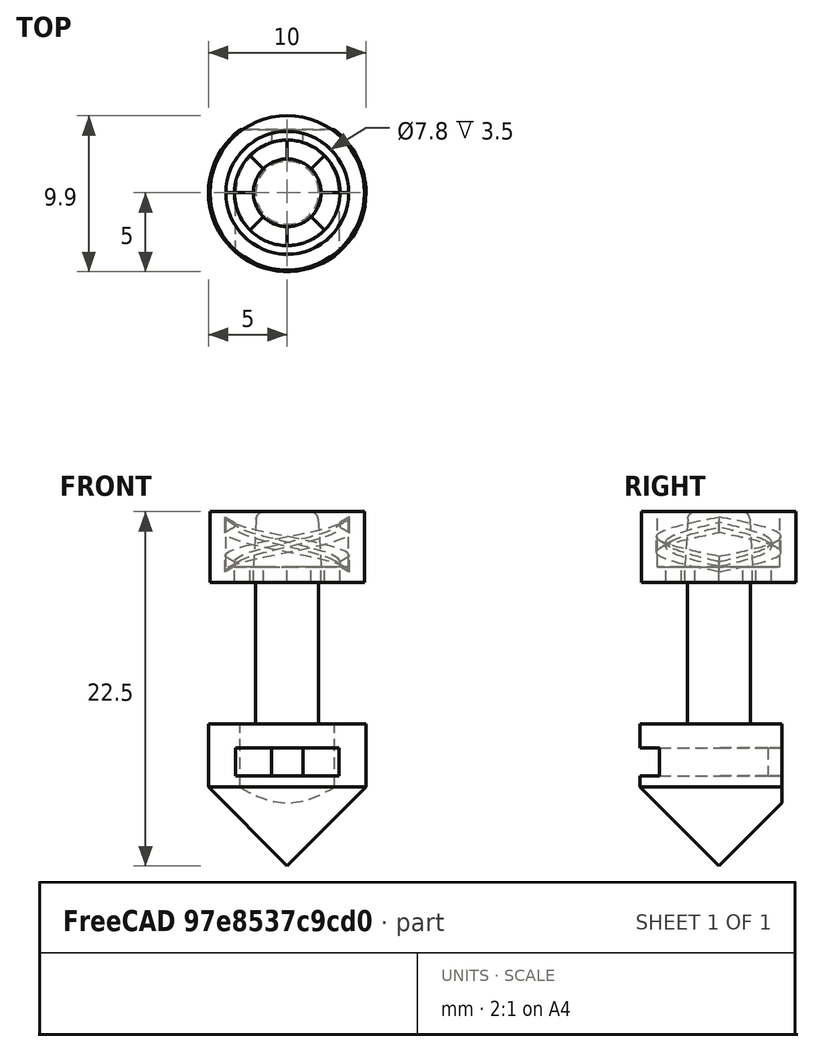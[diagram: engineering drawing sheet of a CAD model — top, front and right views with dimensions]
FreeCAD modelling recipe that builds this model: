
FCSTD DOCUMENT  (FreeCAD 0.19R24344 (Git))
Label: Adapter_Magnet_Luer
Comment: An adapter between the magnet keyed form and a Luer lock for blunt syringe tips.
License: Creative Commons Attribution-NonCommercial-ShareAlike
LicenseURL: http://creativecommons.org/licenses/by-nc-sa/4.0/
objects: Sketcher::SketchObject×12, PartDesign::Pocket×6, PartDesign::Body×4, PartDesign::Revolution×2, PartDesign::ShapeBinder×2, PartDesign::AdditivePipe×2, Mesh::Feature×1
note: 38 computed .brp shape members not serialized (recipe doc carries the construction recipe); baked Part::Feature solids carry a one-line shape summary decoded from their .brp

FEATURE [Sketcher::SketchObject] Sketch
  FullyConstrained = false
  MapMode = 5
  Placement = pos=(0,0,0) rot=(1,0,0;1.5708rad)
  Support = -> [XZ_Plane]
  sketch-geometry (9):
    g0: LineSegment StartX=0 StartY=4.5 StartZ=0 EndX=1.46876 EndY=4.5 EndZ=0
    g1: LineSegment StartX=1.96786 StartY=4.03 StartZ=0 EndX=2.15 EndY=1 EndZ=0
    g2: LineSegment StartX=2.15 StartY=1 StartZ=0 EndX=3.9 EndY=1 EndZ=0
    g3: LineSegment StartX=3.9 StartY=1 StartZ=0 EndX=3.9 EndY=4.5 EndZ=0
    g4: LineSegment StartX=3.9 StartY=4.5 StartZ=0 EndX=4.9 EndY=4.5 EndZ=0
    g5: LineSegment StartX=4.9 StartY=4.5 StartZ=0 EndX=4.9 EndY=0 EndZ=0
    g6: LineSegment StartX=4.9 StartY=0 StartZ=0 EndX=0 EndY=0 EndZ=0
    g7: LineSegment StartX=0 StartY=0 StartZ=0 EndX=0 EndY=4.5 EndZ=0
    g8: ArcOfCircle CenterX=1.46876 CenterY=4 CenterZ=0 NormalX=0 NormalY=0 NormalZ=1 AngleXU=0 Radius=0.5 StartAngle=0.0600393 EndAngle=1.5708
  constraints (25):
    c: PointOnObject(g0,g-2)
    c: Horizontal(g0)
    c: Coincident(g2,g1)
    c: Horizontal(g2)
    c: Coincident(g3,g2)
    c: Vertical(g3)
    c: Coincident(g4,g3)
    c: Horizontal(g4)
    c: Coincident(g5,g4)
    c: PointOnObject(g5,g-1)
    c: Vertical(g5)
    c: Coincident(g6,g5)
    c: Coincident(g6,g-1)
    c: Coincident(g7,g6)
    c: Coincident(g7,g0)
    c: Angle(g0,g1) = 1.63084
    c: DistanceX(g-1,g3) = 3.9
    c: DistanceX(g4,g4) = 1
    c: DistanceY(g3,g3) = 3.5
    c: DistanceY(g5,g5) = 4.5
    c: Tangent(g0,g8) = 1.5708
    c: Tangent(g1,g8) = 1.5708
    c: Radius(g8) = 0.5
    c: DistanceX(g-1,g1) = 2.15
    c: DistanceY(g-1,g0) = 4.5
FEATURE [PartDesign::Revolution] Revolution
  AllowMultiFace = false
  Angle = 360
  Axis = (0,2e-16,1)
  Base = (0,0,0)
  Placement = pos=(0,0,0) rot=(1,0,0;1.5708rad)
  Profile = -> Sketch
  ReferenceAxis = -> Sketch [V_Axis]
  Reversed = true
FEATURE [Sketcher::SketchObject] Sketch001
  FullyConstrained = false
  MapMode = 5
  Placement = pos=(0,0,0) rot=(1,0,0;1.5708rad)
  Support = -> [XZ_Plane]
  sketch-geometry (4):
    g0: LineSegment StartX=3.35 StartY=3.95257 StartZ=0 EndX=3.35 EndY=3.65257 EndZ=0
    g1: LineSegment StartX=3.35 StartY=3.65257 StartZ=0 EndX=3.95 EndY=3.30616 EndZ=0
    g2: LineSegment StartX=3.95 StartY=3.30616 StartZ=0 EndX=3.95 EndY=4.29898 EndZ=0
    g3: LineSegment StartX=3.95 StartY=4.29898 StartZ=0 EndX=3.35 EndY=3.95257 EndZ=0
  constraints (11):
    c: Vertical(g0)
    c: Coincident(g1,g0)
    c: Coincident(g2,g1)
    c: Vertical(g2)
    c: Coincident(g3,g0)
    c: Angle(g0,g3) = 2.0944
    c: Coincident(g2,g3)
    c: Angle(g1,g0) = 2.0944
    c: DistanceY(g0,g0) = 0.3
    c: DistanceX(g0,g2) = 0.6
    c: DistanceX(g-1,g0) = 3.35
FEATURE [Sketcher::SketchObject] Sketch002
  FullyConstrained = false
  MapMode = 5
  Placement = pos=(0,0,0) rot=(1,0,0;3.14159rad)
  Support = -> [Revolution]
  sketch-geometry (5):
    g0: LineSegment StartX=-2.15 StartY=3e-16 StartZ=0 EndX=-3.35 EndY=4e-16 EndZ=0
    g1: ArcOfCircle CenterX=0 CenterY=0 CenterZ=0 NormalX=0 NormalY=0 NormalZ=1 AngleXU=0 Radius=2.15 StartAngle=2.35619 EndAngle=3.14159
    g2: ArcOfCircle CenterX=0 CenterY=0 CenterZ=0 NormalX=0 NormalY=0 NormalZ=1 AngleXU=0 Radius=3.35 StartAngle=2.35619 EndAngle=3.14159
    g3: LineSegment StartX=-2.36881 StartY=2.36881 StartZ=0 EndX=-1.52028 EndY=1.52028 EndZ=0
    g4: LineSegment StartX=-2.36881 StartY=2.36881 StartZ=0 EndX=0 EndY=0 EndZ=0
  constraints (14):
    c: PointOnObject(g0,g-1)
    c: PointOnObject(g0,g-1)
    c: Coincident(g2,g0)
    c: Coincident(g1,g0)
    c: Coincident(g2,g3)
    c: Coincident(g3,g1)
    c: Coincident(g1,g-1)
    c: Coincident(g2,g1)
    c: Radius(g2) = 3.35
    c: Radius(g1) = 2.15
    c: Coincident(g4,g2)
    c: Coincident(g4,g1)
    c: Parallel(g4,g3)
    c: Angle(g3,g0) = 0.785398
FEATURE [Sketcher::SketchObject] Sketch003
  FullyConstrained = false
  MapMode = 5
  Placement = pos=(0,0,0) rot=(1,0,0;3.14159rad)
  Support = -> [Revolution]
  sketch-geometry (5):
    g0: LineSegment StartX=1e-16 StartY=2.15 StartZ=0 EndX=2e-16 EndY=3.35 EndZ=0
    g1: ArcOfCircle CenterX=0 CenterY=0 CenterZ=0 NormalX=0 NormalY=0 NormalZ=1 AngleXU=0 Radius=2.15 StartAngle=0.785398 EndAngle=1.5708
    g2: ArcOfCircle CenterX=0 CenterY=0 CenterZ=0 NormalX=0 NormalY=0 NormalZ=1 AngleXU=0 Radius=3.35 StartAngle=0.785398 EndAngle=1.5708
    g3: LineSegment StartX=2.36881 StartY=2.36881 StartZ=0 EndX=1.52028 EndY=1.52028 EndZ=0
    g4: LineSegment StartX=2.36881 StartY=2.36881 StartZ=0 EndX=0 EndY=0 EndZ=0
  constraints (14):
    c: Coincident(g2,g3)
    c: Coincident(g3,g1)
    c: Coincident(g1,g-1)
    c: Coincident(g2,g1)
    c: Radius(g2) = 3.35
    c: Radius(g1) = 2.15
    c: Coincident(g4,g2)
    c: Coincident(g4,g1)
    c: Parallel(g4,g3)
    c: Angle(g3,g0) = 0.785398
    c: Coincident(g0,g2)
    c: Coincident(g1,g0)
    c: PointOnObject(g0,g-2)
    c: PointOnObject(g0,g-2)
FEATURE [Sketcher::SketchObject] Sketch004
  FullyConstrained = false
  MapMode = 5
  Placement = pos=(0,0,0) rot=(1,0,0;3.14159rad)
  Support = -> [Revolution]
  sketch-geometry (5):
    g0: LineSegment StartX=2.15 StartY=0 StartZ=0 EndX=3.35 EndY=-8e-16 EndZ=0
    g1: ArcOfCircle CenterX=0 CenterY=0 CenterZ=0 NormalX=0 NormalY=0 NormalZ=1 AngleXU=0 Radius=2.15 StartAngle=5.49779 EndAngle=6.28319
    g2: ArcOfCircle CenterX=0 CenterY=0 CenterZ=0 NormalX=0 NormalY=0 NormalZ=1 AngleXU=0 Radius=3.35 StartAngle=5.49779 EndAngle=6.28319
    g3: LineSegment StartX=2.36881 StartY=-2.36881 StartZ=0 EndX=1.52028 EndY=-1.52028 EndZ=0
    g4: LineSegment StartX=2.36881 StartY=-2.36881 StartZ=0 EndX=0 EndY=0 EndZ=0
  constraints (14):
    c: Coincident(g2,g0)
    c: Coincident(g1,g0)
    c: Coincident(g2,g3)
    c: Coincident(g3,g1)
    c: Coincident(g1,g-1)
    c: Coincident(g2,g1)
    c: Radius(g2) = 3.35
    c: Radius(g1) = 2.15
    c: Coincident(g4,g2)
    c: Coincident(g4,g1)
    c: Parallel(g4,g3)
    c: Angle(g3,g0) = 0.785398
    c: PointOnObject(g0,g-1)
    c: PointOnObject(g0,g-1)
FEATURE [Sketcher::SketchObject] Sketch005
  FullyConstrained = false
  MapMode = 5
  Placement = pos=(0,0,0) rot=(1,0,0;3.14159rad)
  Support = -> [Revolution]
  sketch-geometry (5):
    g0: LineSegment StartX=-4e-16 StartY=-2.15 StartZ=0 EndX=-6e-16 EndY=-3.35 EndZ=0
    g1: ArcOfCircle CenterX=0 CenterY=0 CenterZ=0 NormalX=0 NormalY=0 NormalZ=1 AngleXU=0 Radius=2.15 StartAngle=3.92699 EndAngle=4.71239
    g2: ArcOfCircle CenterX=0 CenterY=0 CenterZ=0 NormalX=0 NormalY=0 NormalZ=1 AngleXU=0 Radius=3.35 StartAngle=3.92699 EndAngle=4.71239
    g3: LineSegment StartX=-2.36881 StartY=-2.36881 StartZ=0 EndX=-1.52028 EndY=-1.52028 EndZ=0
    g4: LineSegment StartX=-2.36881 StartY=-2.36881 StartZ=0 EndX=0 EndY=0 EndZ=0
  constraints (14):
    c: Coincident(g2,g0)
    c: Coincident(g1,g0)
    c: Coincident(g2,g3)
    c: Coincident(g3,g1)
    c: Coincident(g1,g-1)
    c: Coincident(g2,g1)
    c: Radius(g2) = 3.35
    c: Radius(g1) = 2.15
    c: Coincident(g4,g2)
    c: Coincident(g4,g1)
    c: Parallel(g4,g3)
    c: Angle(g3,g0) = 0.785398
    c: PointOnObject(g0,g-2)
    c: PointOnObject(g0,g-2)
FEATURE [PartDesign::Pocket] Pocket
  AllowMultiFace = false
  BaseFeature = -> Revolution
  Length = 5
  Length2 = 100
  Placement = pos=(0,0,0) rot=(1,0,0;1.5708rad)
  Profile = -> Sketch002
  Type = 1
FEATURE [PartDesign::Pocket] Pocket001
  AllowMultiFace = false
  BaseFeature = -> Pocket
  Length = 5
  Length2 = 100
  Placement = pos=(0,0,0) rot=(1,0,0;1.5708rad)
  Profile = -> Sketch003
  Type = 1
FEATURE [PartDesign::Pocket] Pocket002
  AllowMultiFace = false
  BaseFeature = -> Pocket001
  Length = 5
  Length2 = 100
  Placement = pos=(0,0,0) rot=(1,0,0;1.5708rad)
  Profile = -> Sketch004
  Type = 1
FEATURE [PartDesign::Pocket] Pocket003
  AllowMultiFace = false
  BaseFeature = -> Pocket002
  Length = 5
  Length2 = 100
  Placement = pos=(0,0,0) rot=(1,0,0;1.5708rad)
  Profile = -> Sketch005
  Type = 1
FEATURE [Sketcher::SketchObject] Sketch006
  FullyConstrained = true
  MapMode = 5
  Placement = pos=(0,0,0) rot=(1,0,0;3.14159rad)
  Support = -> [Pocket003]
FEATURE [PartDesign::Body] Body  label="Luer body"
  Group = -> [Sketch,Revolution,Sketch001,Pocket,Pocket001,Pocket002,Pocket003,Sketch006]
  Origin = -> Origin
  Tip = -> Pocket003
FEATURE [Sketcher::SketchObject] Sketch007
  FullyConstrained = false
  MapMode = 5
  Placement = pos=(0,0,0) rot=(1,0,0;1.5708rad)
  Support = -> [XZ_Plane004]
  sketch-geometry (6):
    g0: LineSegment StartX=0 StartY=0 StartZ=0 EndX=0 EndY=-18 EndZ=0
    g1: LineSegment StartX=0 StartY=-18 StartZ=0 EndX=5 EndY=-13 EndZ=0
    g2: LineSegment StartX=5 StartY=-13 StartZ=0 EndX=5 EndY=-9 EndZ=0
    g3: LineSegment StartX=5 StartY=-9 StartZ=0 EndX=2 EndY=-9 EndZ=0
    g4: LineSegment StartX=2 StartY=-9 StartZ=0 EndX=2 EndY=0 EndZ=0
    g5: LineSegment StartX=2 StartY=0 StartZ=0 EndX=0 EndY=0 EndZ=0
  constraints (17):
    c: Coincident(g0,g-1)
    c: Vertical(g0)
    c: Coincident(g1,g0)
    c: Coincident(g2,g1)
    c: Vertical(g2)
    c: Horizontal(g3)
    c: PointOnObject(g4,g-1)
    c: Vertical(g4)
    c: Coincident(g5,g4)
    c: Coincident(g5,g0)
    c: Coincident(g2,g3)
    c: Coincident(g3,g4)
    c: DistanceY(g4,g4) = 9
    c: DistanceX(g-1,g2) = 5
    c: DistanceY(g2,g2) = 4
    c: DistanceY(g0,g1) = 5
    c: DistanceX(g-1,g3) = 2
FEATURE [PartDesign::Revolution] Revolution001
  AllowMultiFace = false
  Angle = 360
  Axis = (0,2e-16,1)
  Base = (0,0,0)
  Placement = pos=(0,0,0) rot=(1,0,0;1.5708rad)
  Profile = -> Sketch007
  ReferenceAxis = -> Sketch007 [V_Axis]
  Reversed = true
FEATURE [Sketcher::SketchObject] Sketch008
  FullyConstrained = false
  MapMode = 5
  Placement = pos=(0,-4e-15,-9) rot=(0,0,1;3.14159rad)
  Support = -> [Revolution001]
  sketch-geometry (4):
    g0: LineSegment StartX=-5 StartY=-4 StartZ=0 EndX=5 EndY=-4 EndZ=0
    g1: LineSegment StartX=5 StartY=-4 StartZ=0 EndX=5 EndY=-5.5 EndZ=0
    g2: LineSegment StartX=5 StartY=-5.5 StartZ=0 EndX=-5 EndY=-5.5 EndZ=0
    g3: LineSegment StartX=-5 StartY=-5.5 StartZ=0 EndX=-5 EndY=-4 EndZ=0
  constraints (12):
    c: Coincident(g0,g1)
    c: Coincident(g1,g2)
    c: Coincident(g2,g3)
    c: Coincident(g3,g0)
    c: Horizontal(g0)
    c: Horizontal(g2)
    c: Vertical(g1)
    c: Vertical(g3)
    c: DistanceY(g0,g-1) = 4
    c: Distance(g0) = 10
    c: Distance(g3) = 1.5
    c: DistanceX(g2,g-1) = 5
FEATURE [PartDesign::Pocket] Pocket004
  AllowMultiFace = false
  BaseFeature = -> Revolution001
  Length = 5
  Length2 = 100
  Placement = pos=(0,0,0) rot=(1,0,0;1.5708rad)
  Profile = -> Sketch008
  Type = 1
FEATURE [Sketcher::SketchObject] Sketch009
  AttachmentOffset = pos=(0,0,-1.5) rot=(0,0,1;0rad)
  FullyConstrained = false
  MapMode = 5
  Placement = pos=(0,-4.6e-15,-10.5) rot=(0,0,1;3.14159rad)
  Support = -> [Pocket004]
  sketch-geometry (8):
    g0: ArcOfCircle CenterX=0 CenterY=0 CenterZ=0 NormalX=0 NormalY=0 NormalZ=1 AngleXU=0 Radius=3.275 StartAngle=3.14159 EndAngle=4.40209
    g1: LineSegment StartX=-3.275 StartY=4e-16 StartZ=0 EndX=-3.275 EndY=6.5 EndZ=0
    g2: LineSegment StartX=-3.275 StartY=6.5 StartZ=0 EndX=3.27 EndY=6.5 EndZ=0
    g3: LineSegment StartX=3.27 StartY=6.5 StartZ=0 EndX=3.27 EndY=-9e-16 EndZ=0
    g4: ArcOfCircle CenterX=0 CenterY=0 CenterZ=0 NormalX=0 NormalY=0 NormalZ=1 AngleXU=0 Radius=3.27 StartAngle=5.02318 EndAngle=6.28319
    g5: LineSegment StartX=-1 StartY=-3.11859 StartZ=0 EndX=-1 EndY=-6.5 EndZ=0
    g6: LineSegment StartX=-1 StartY=-6.5 StartZ=0 EndX=1 EndY=-6.5 EndZ=0
    g7: LineSegment StartX=1 StartY=-6.5 StartZ=0 EndX=1 EndY=-3.11334 EndZ=0
  constraints (22):
    c: Coincident(g0,g-1)
    c: Coincident(g2,g1)
    c: Horizontal(g2)
    c: Coincident(g3,g2)
    c: Radius(g0) = 3.275
    c: Tangent(g1,g0) = 1.5708
    c: Vertical(g1)
    c: DistanceY(g-1,g1) = 6.5
    c: Coincident(g4,g0)
    c: Vertical(g5)
    c: Coincident(g6,g5)
    c: Horizontal(g6)
    c: Coincident(g7,g6)
    c: Vertical(g7)
    c: Radius(g4) = 3.27
    c: Coincident(g4,g7)
    c: DistanceX(g5,g-1) = 1
    c: DistanceX(g-1,g6) = 1
    c: PointOnObject(g3,g-1)
    c: Tangent(g4,g3) = 1.5708
    c: Coincident(g0,g5)
    c: DistanceY(g5,g-1) = 6.5
FEATURE [PartDesign::Pocket] Pocket005
  AllowMultiFace = false
  BaseFeature = -> Pocket004
  Length = 1.8
  Length2 = 100
  Placement = pos=(0,0,0) rot=(1,0,0;1.5708rad)
  Profile = -> Sketch009
  Type = 0
FEATURE [PartDesign::Body] Body003  label="Magnet holder"
  Group = -> [Sketch007,Revolution001,Sketch008,Pocket004,Sketch009,Pocket005]
  Origin = -> Origin003
  Tip = -> Pocket005
FEATURE [Sketcher::SketchObject] CopyCopySketch004
  FullyConstrained = false
  Placement = pos=(0,0,0) rot=(1,0,0;1.5708rad)
  sketch-geometry (8):
    g0: LineSegment StartX=3.35 StartY=1.4869 StartZ=0 EndX=3.35 EndY=1.1869 EndZ=0
    g1: LineSegment StartX=3.35 StartY=1.1869 StartZ=0 EndX=3.95 EndY=0.840494 EndZ=0
    g2: LineSegment StartX=3.95 StartY=0.840494 StartZ=0 EndX=3.95 EndY=1.83331 EndZ=0
    g3: LineSegment StartX=3.95 StartY=1.83331 StartZ=0 EndX=3.35 EndY=1.4869 EndZ=0
    g4: LineSegment StartX=-3.35 StartY=1.4869 StartZ=0 EndX=-3.35 EndY=1.1869 EndZ=0
    g5: LineSegment StartX=-3.35 StartY=1.1869 StartZ=0 EndX=-3.95 EndY=0.840494 EndZ=0
    g6: LineSegment StartX=-3.95 StartY=0.840494 StartZ=0 EndX=-3.95 EndY=1.83331 EndZ=0
    g7: LineSegment StartX=-3.95 StartY=1.83331 StartZ=0 EndX=-3.35 EndY=1.4869 EndZ=0
  constraints (19):
    c: Vertical(g0)
    c: Coincident(g1,g0)
    c: Coincident(g2,g1)
    c: Vertical(g2)
    c: Coincident(g3,g0)
    c: Angle(g0,g3) = 2.0944
    c: Coincident(g2,g3)
    c: Angle(g1,g0) = 2.0944
    c: DistanceY(g0,g0) = 0.3
    c: DistanceX(g0,g2) = 0.6
    c: DistanceX(g-1,g0) = 3.35
    c: Coincident(g5,g4)
    c: Coincident(g7,g4)
    c: Symmetric(g0,g4,g-2)
    c: Symmetric(g6,g2,g-2)
    c: Coincident(g7,g6)
    c: Symmetric(g4,g0,g-2)
    c: Coincident(g5,g6)
    c: Symmetric(g1,g5,g-2)
FEATURE [PartDesign::ShapeBinder] CopyHelix001001
  TraceSupport = false
FEATURE [PartDesign::AdditivePipe] AdditivePipe002
  AllowMultiFace = false
  AuxilleryCurvelinear = true
  AuxillerySpineTangent = false
  Binormal = (0,0,0)
  Mode = 2
  Placement = pos=(0,0,0) rot=(1,0,0;1.5708rad)
  Profile = -> CopyCopySketch004
  Spine = -> CopyHelix001001
  SpineTangent = false
  Transformation = 1
  Transition = 0
FEATURE [PartDesign::Body] Body004  label="Luer Lock 1"
  Group = -> [AdditivePipe002,CopyHelix001001]
  Origin = -> Origin004
  Tip = -> AdditivePipe002
FEATURE [PartDesign::ShapeBinder] CopyHelix001002
  TraceSupport = false
FEATURE [Sketcher::SketchObject] CopyCopySketch006
  FullyConstrained = false
  Placement = pos=(0,0,0) rot=(1,0,0;1.5708rad)
  sketch-geometry (8):
    g0: LineSegment StartX=3.35 StartY=1.4869 StartZ=0 EndX=3.35 EndY=1.1869 EndZ=0
    g1: LineSegment StartX=3.35 StartY=1.1869 StartZ=0 EndX=3.95 EndY=0.840494 EndZ=0
    g2: LineSegment StartX=3.95 StartY=0.840494 StartZ=0 EndX=3.95 EndY=1.83331 EndZ=0
    g3: LineSegment StartX=3.95 StartY=1.83331 StartZ=0 EndX=3.35 EndY=1.4869 EndZ=0
    g4: LineSegment StartX=-3.35 StartY=1.4869 StartZ=0 EndX=-3.35 EndY=1.1869 EndZ=0
    g5: LineSegment StartX=-3.35 StartY=1.1869 StartZ=0 EndX=-3.95 EndY=0.840494 EndZ=0
    g6: LineSegment StartX=-3.95 StartY=0.840494 StartZ=0 EndX=-3.95 EndY=1.83331 EndZ=0
    g7: LineSegment StartX=-3.95 StartY=1.83331 StartZ=0 EndX=-3.35 EndY=1.4869 EndZ=0
  constraints (19):
    c: Vertical(g0)
    c: Coincident(g1,g0)
    c: Coincident(g2,g1)
    c: Vertical(g2)
    c: Coincident(g3,g0)
    c: Angle(g0,g3) = 2.0944
    c: Coincident(g2,g3)
    c: Angle(g1,g0) = 2.0944
    c: DistanceY(g0,g0) = 0.3
    c: DistanceX(g0,g2) = 0.6
    c: DistanceX(g-1,g0) = 3.35
    c: Coincident(g5,g4)
    c: Coincident(g7,g4)
    c: Symmetric(g0,g4,g-2)
    c: Symmetric(g6,g2,g-2)
    c: Coincident(g7,g6)
    c: Symmetric(g4,g0,g-2)
    c: Coincident(g5,g6)
    c: Symmetric(g1,g5,g-2)
FEATURE [PartDesign::AdditivePipe] AdditivePipe003
  AllowMultiFace = false
  AuxilleryCurvelinear = true
  AuxillerySpineTangent = false
  Binormal = (0,0,0)
  Mode = 2
  Placement = pos=(0,0,0) rot=(1,0,0;1.5708rad)
  Profile = -> CopyCopySketch006
  Spine = -> CopyHelix001002
  SpineTangent = false
  Transformation = 1
  Transition = 0
FEATURE [PartDesign::Body] Body005  label="Luer Lock 2"
  Group = -> [AdditivePipe003,CopyHelix001002]
  Origin = -> Origin005
  Placement = pos=(0,0,0) rot=(0,0,1;3.14159rad)
  Tip = -> AdditivePipe003
FEATURE [Mesh::Feature] Mesh004  label="Built-in fine mesh"
